# Revit family: ПСК-50
name_source: partatom
category: Арматура трубопроводов
units: mm (PartAtom-declared; Revit-internal decimal feet)

## family parameters
Всегда вертикально = Да
На основе рабочей плоскости = Нет
Общий = Нет
При загрузке вырезать с полостями = Нет
Размер круглого соединителя = Использовать диаметр
Тип детали = Клапан - Вставляется

## types (17) — shared parameters
ADSK_Единица измерения = шт.
ADSK_Завод-изготовитель = РУП "БЕЛГАЗТЕХНИКА"
ADSK_Класс герметичности по ГОСТ 9544-2005 = А
ADSK_Количество = 1
ADSK_Коэффициент расхода, а = 0,3
ADSK_Марка = ПСК-50
ADSK_Тип соединения = фланцевое
zero-valued in all types: Отметка по умолчанию

## per-type parameters (varying)
| type | ADSK_Диапазоны контролируемого давления (Pк), Мпа | ADSK_Масса_Текст | ADSK_Материал наименование | ADSK_Наименование |
| алюминиевый сплав исполнение 00 | 0,0016-0,003 | 9,0 кг | АК 12 | Клапан предохранительный сбросной DN 50 ПСК-50-00-АК ТУ BY 100270876.155-2010 |
| алюминиевый сплав исполнение 01 | 0,003-0,007 | 9,0 кг | АК 12 | Клапан предохранительный сбросной DN 50 ПСК-50-01-АК ТУ BY 100270876.155-2010 |
| алюминиевый сплав исполнение 02 | 0,007-0,02 | 9,0 кг | АК 12 | Клапан предохранительный сбросной DN 50 ПСК-50-02-АК ТУ BY 100270876.155-2010 |
| алюминиевый сплав исполнение 03 | 0,02-0,05 | 9,0 кг | АК 12 | Клапан предохранительный сбросной DN 50 ПСК-50-03-АК ТУ BY 100270876.155-2010 |
| алюминиевый сплав исполнение 04 | 0,05-0,15 | 9,0 кг | АК 12 | Клапан предохранительный сбросной DN 50 ПСК-50-04-АК ТУ BY 100270876.155-2010 |
| алюминиевый сплав исполнение 05 | 0,15-0,6 | 9,0 кг | АК 12 | Клапан предохранительный сбросной DN 50 ПСК-50-05-АК ТУ BY 100270876.155-2010 |
| серый чугун исполнение 00 | 0,0016-0,003 | 20,0 кг | СЧ 20 | Клапан предохранительный сбросной DN 50 ПСК-50-00-СЧ ТУ BY 100270876.155-2010 |
| высокопрочный чугун исполнение 00 | 0,0016-0,003 | 20,0 кг | ВЧ 40 | Клапан предохранительный сбросной DN 50 ПСК-50-00-ВЧ ТУ BY 100270876.155-2010 |
| серый чугун исполнение 01 | 0,003-0,007 | 20,0 кг | СЧ 20 | Клапан предохранительный сбросной DN 50 ПСК-50-01-СЧ ТУ BY 100270876.155-2010 |
| серый чугун исполнение 02 | 0,007-0,02 | 20,0 кг | СЧ 20 | Клапан предохранительный сбросной DN 50 ПСК-50-02-СЧ ТУ BY 100270876.155-2010 |
| серый чугун исполнение 03 | 0,02-0,05 | 20,0 кг | СЧ 20 | Клапан предохранительный сбросной DN 50 ПСК-50-03-СЧ ТУ BY 100270876.155-2010 |
| серый чугун исполнение 04 | 0,05-0,15 | 20,0 кг | СЧ 20 | Клапан предохранительный сбросной DN 50 ПСК-50-04-СЧ ТУ BY 100270876.155-2010 |
| высокопрочный чугун исполнение 01 | 0,003-0,007 | 20,0 кг | ВЧ 40 | Клапан предохранительный сбросной DN 50 ПСК-50-01-ВЧ ТУ BY 100270876.155-2010 |
| высокопрочный чугун исполнение 02 | 0,007-0,02 | 20,0 кг | ВЧ 40 | Клапан предохранительный сбросной DN 50 ПСК-50-02-ВЧ ТУ BY 100270876.155-2010 |
| высокопрочный чугун исполнение 03 | 0,02-0,05 | 20,0 кг | ВЧ 40 | Клапан предохранительный сбросной DN 50 ПСК-50-03-ВЧ ТУ BY 100270876.155-2010 |
| высокопрочный чугун исполнение 04 | 0,05-0,15 | 20,0 кг | ВЧ 40 | Клапан предохранительный сбросной DN 50 ПСК-50-04-ВЧ ТУ BY 100270876.155-2010 |
| высокопрочный чугун исполнение 05 | 0,15-0,6 | 20,0 кг | ВЧ 40 | Клапан предохранительный сбросной DN 50 ПСК-50-05-ВЧ ТУ BY 100270876.155-2010 |
